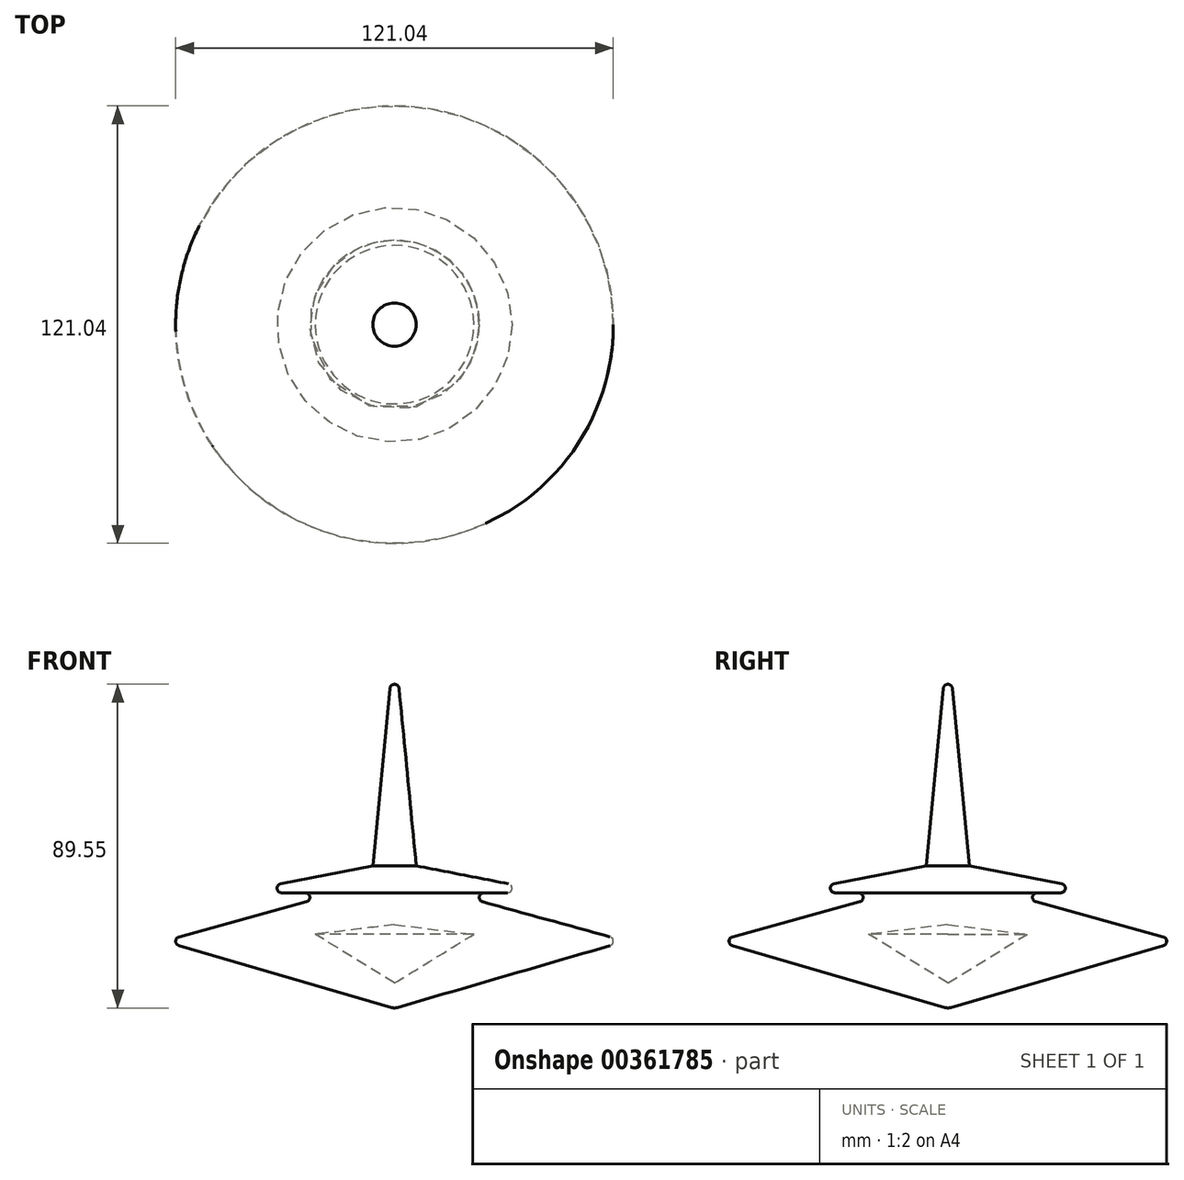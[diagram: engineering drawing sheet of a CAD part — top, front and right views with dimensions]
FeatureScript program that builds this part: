
annotation { "Feature Type Name" : "Feature", "Feature Type Description" : "" }
export const myFeature = defineFeature(function(context is Context, id is Id, definition is map)
    precondition{}
    {
        {
            var Q0;
            Q0=qCreatedBy(makeId("Front.planeOp"),FACE);
            var sketch = newSketch(context, id + "F0", { "sketchPlane" : qUnion([Q0])});
            skLineSegment(sketch, "E0", {"start": v(0.7, -112.36) * mm, "end": v(59.6, -95.22) * mm});
            skLineSegment(sketch, "E1", {"start": v(59.59, -92.78) * mm, "end": v(24.35, -83.1) * mm});
            skLineSegment(sketch, "E2", {"start": v(24.69, -80.61) * mm, "end": v(31.21, -80.61) * mm});
            skLineSegment(sketch, "E3", {"start": v(31.45, -78.1) * mm, "end": v(6, -73.13) * mm});
            skLineSegment(sketch, "E4", {"start": v(6, -73.13) * mm, "end": v(1.26, -24.07) * mm});
            skLineSegment(sketch, "E5", {"start": v(0, -10.97) * mm, "end": v(0, -89.42) * mm});
            skPoint(sketch, "E6.visualSharp", {"position": v(44.36, -80.61) * mm});
            skArc(sketch, "E6.filletArc", {"start": v(31.21, -80.61) * mm, "mid": v(32.47, -79.46) * mm, "end": v(31.45, -78.1) * mm});
            skPoint(sketch, "E7.visualSharp", {"position": v(63.92, -93.97) * mm});
            skArc(sketch, "E7.filletArc", {"start": v(59.6, -95.22) * mm, "mid": v(60.52, -94) * mm, "end": v(59.59, -92.78) * mm});
            skPoint(sketch, "E8.visualSharp", {"position": v(15.26, -80.61) * mm});
            skArc(sketch, "E8.filletArc", {"start": v(24.69, -80.61) * mm, "mid": v(23.43, -81.71) * mm, "end": v(24.35, -83.1) * mm});
            skLineSegment(sketch, "E9.MirrorCS", {"start": v(-6, -73.13) * mm, "end": v(-1.26, -24.07) * mm});
            skLineSegment(sketch, "E10.MirrorCS", {"start": v(-31.45, -78.1) * mm, "end": v(-6, -73.13) * mm});
            skLineSegment(sketch, "E11.MirrorCS", {"start": v(-59.59, -92.78) * mm, "end": v(-24.35, -83.1) * mm});
            skLineSegment(sketch, "E12.MirrorCS", {"start": v(-0.7, -112.36) * mm, "end": v(-59.6, -95.22) * mm});
            skArc(sketch, "E13.MirrorCS", {"start": v(-24.69, -80.61) * mm, "mid": v(-23.43, -81.71) * mm, "end": v(-24.35, -83.1) * mm});
            skArc(sketch, "E14.MirrorCS", {"start": v(-31.21, -80.61) * mm, "mid": v(-32.47, -79.46) * mm, "end": v(-31.45, -78.1) * mm});
            skArc(sketch, "E15.MirrorCS", {"start": v(-59.6, -95.22) * mm, "mid": v(-60.52, -94) * mm, "end": v(-59.59, -92.78) * mm});
            skLineSegment(sketch, "E16.MirrorCS", {"start": v(-24.69, -80.61) * mm, "end": v(-31.21, -80.61) * mm});
            skPoint(sketch, "E17.visualSharp", {"position": v(0, -112.57) * mm});
            skArc(sketch, "E17.filletArc", {"start": v(-0.7, -112.36) * mm, "mid": v(0, -112.47) * mm, "end": v(0.7, -112.36) * mm});
            skPoint(sketch, "E18.visualSharp", {"position": v(0, -10.97) * mm});
            skArc(sketch, "E18.filletArc", {"start": v(1.26, -24.07) * mm, "mid": v(0, -22.92) * mm, "end": v(-1.26, -24.07) * mm});
            skLineSegment(sketch, "E19", {"start": v(0, -89.42) * mm, "end": v(21.92, -92.07) * mm});
            skLineSegment(sketch, "E20", {"start": v(21.92, -92.07) * mm, "end": v(0, -105.58) * mm});
            skLineSegment(sketch, "E21.MirrorCS", {"start": v(0, -89.42) * mm, "end": v(-21.92, -92.07) * mm});
            skLineSegment(sketch, "E22.MirrorCS", {"start": v(-21.92, -92.07) * mm, "end": v(0, -105.58) * mm});
            skLineSegment(sketch, "E23.trimOffspring", {"start": v(0, -105.58) * mm, "end": v(0, -112.57) * mm});
            skSolve(sketch);
        }
        {
            var Q0;
            Q0=makeQuery(id+"F0.imprint","IMPRINT",FACE,{"disambiguationData":[TD([[makeQuery(id+"F0.imprint","IMPRINT",EDGE,{"derivedFrom":sQuery(id+"F0.wireOp",EDGE,"E0")}),1.0]])]});
            var Q1;
            Q1=sQuery(id+"F0.wireOp",EDGE,"E5");
            revolve(context, id + "F1", {"entities" : qUnion([Q0]), "axis" : qUnion([Q1]), "revolveType" : RevolveType.FULL});
        }
        {
            var Q0;
            {var subQ6=sQuery(id+"F0.wireOp",EDGE,"E9.MirrorCS");Q0=makeQuery(id+"F0.imprint","IMPRINT",FACE,{"disambiguationData":[TD([[makeQuery(id+"F0.imprint","IMPRINT",EDGE,{"derivedFrom":subQ6}),-1.0]])]});}
            var Q1;
            Q1=sQuery(id+"F0.wireOp",EDGE,"E5");
            revolve(context, id + "F2", {"entities" : qUnion([Q0]), "axis" : qUnion([Q1]), "revolveType" : RevolveType.FULL});
        }
    });
